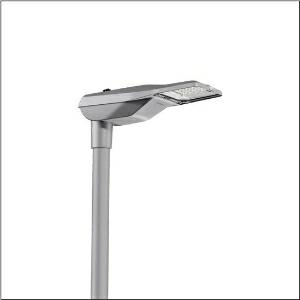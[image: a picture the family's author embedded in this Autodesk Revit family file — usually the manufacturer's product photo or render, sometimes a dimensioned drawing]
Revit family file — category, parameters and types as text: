
# Revit family: streetlight_sl_21_micro___st1_0ab_5xe1m33s08db_765d
name_source: partatom
category: Lighting Fixtures
units: mm (PartAtom-declared; Revit-internal decimal feet)

## family parameters
Cut with Voids When Loaded = No
Host = Face
Light Source = No
Part Type = Normal
Room Calculation Point = No
Round Connector Dimension = Use Diameter
Shared = No

## types (1)
- --- (1 x LED, 4500 lm, 39.1 W, 3000K)
    Apparent Load = 39 VA
    CIE Flux Codes = 38 73 97 100 100
    Color Rendering = 70
    Color Temperature = 3000K
    Default Elevation = 1800 mm
    Description = Streetlight SL 21 micro, mast luminaire, primary light control with lens, of PMMA, primary optical cover: cover, of toughened safety glass, transparent, light distribution: ST1.0aB, light emission: direct distribution, primary light characteristic: asymmetric, installation type: side-entry, post-top, LED, High Power LED, rated luminous flux: 4.500lm, luminous efficacy: 115lm/W, light colour: 730, colour temperature: 3000K, control gear: D4i, control: flexible luminous flux parameterisation, time-dependent luminous flux control, constant luminous flux control, overheat protection, pre-setting: logarithmic dimming characteristic, mains connection: 220..240V, AC, 50/60Hz, start of lifetime: 39W, end of service life: 41W, reduction: 18W, luminaire housing, of diecast aluminium, powder-coated, SITECO metallic grey (DB 702S), corrosivity category C5 high according to DIN EN ISO 12944, please order mast flange separately, inclination adjustable: 0°, 5°, 10°, 15°, sealing non-destructively replaceable, multi-level sealing system, length: 528mm, width: 235mm, height: 110mm, mast flange for spigot size: 42mm (side-entry): 5XC10008XM4, 60/48mm (side-entry/post-top): 5XC10108XM2, 76/60mm (side-entry/post-top): 5XC10108XM1, Smart Interface above, protection rating (complete): IP66, insulation class (complete): insulation class II (safety insulation), certification: CE, ENEC, ENEC+, VDE, impact resistance: IK10, permissible operating ambient temperature for outdoor applications: -40..+50°C, standard-compliant lighting for roads and squares, packaging unit: 1 piece

Light Distribution: ST1.0aB
    Height = 110 mm
    Lamp = 1 x LED
    Lamp Light Flux = 4500 lm
    Lamp Power = 39.1 W
    Lamp count = 1
    Length = 528 mm
    Luminous efficacy = 115 lm/W
    Manufacturer = Siteco
    ModVariant = No
    Model = 5XE1M33S08DB
    Number of Poles = 1
    OnlyDefault = Yes
    Power Factor = 1
    Product Name = Streetlight SL 21 micro | ST1.0aB
    Product group = mast luminaire | pylon top
    ProductGroupID = 6100
    Protection Class = Protection class II
    Protection Degree = IP 66
    RLX_Detail_Level = 1
    RLX_Emergency_Light_Flux = 0 lm
    RLX_Emergency_Type = 0
    RLX_Emergency_Type_DB = No
    RlxData = <blob elided: 98329 chars, md5=7a4f3b00>
    Socket = socket
    Standby Power = 0 W
    System Light Flux = 4500 lm
    System Power = 39 W
    Type Comments = factory setting: luminous flux: 100 % | dim-lin: 254 | 765 mA
    Type Image = l_1277292.jpg
    URL = http://relux.com
    VarID = @adj_153469
    Voltage = 0 V
    Weight = 0.00 kg
    Width = 235 mm

## geometry (parser evidence)
native form markers: Blend x4, Sweep x10
no freeform markers — native parametric forms only
